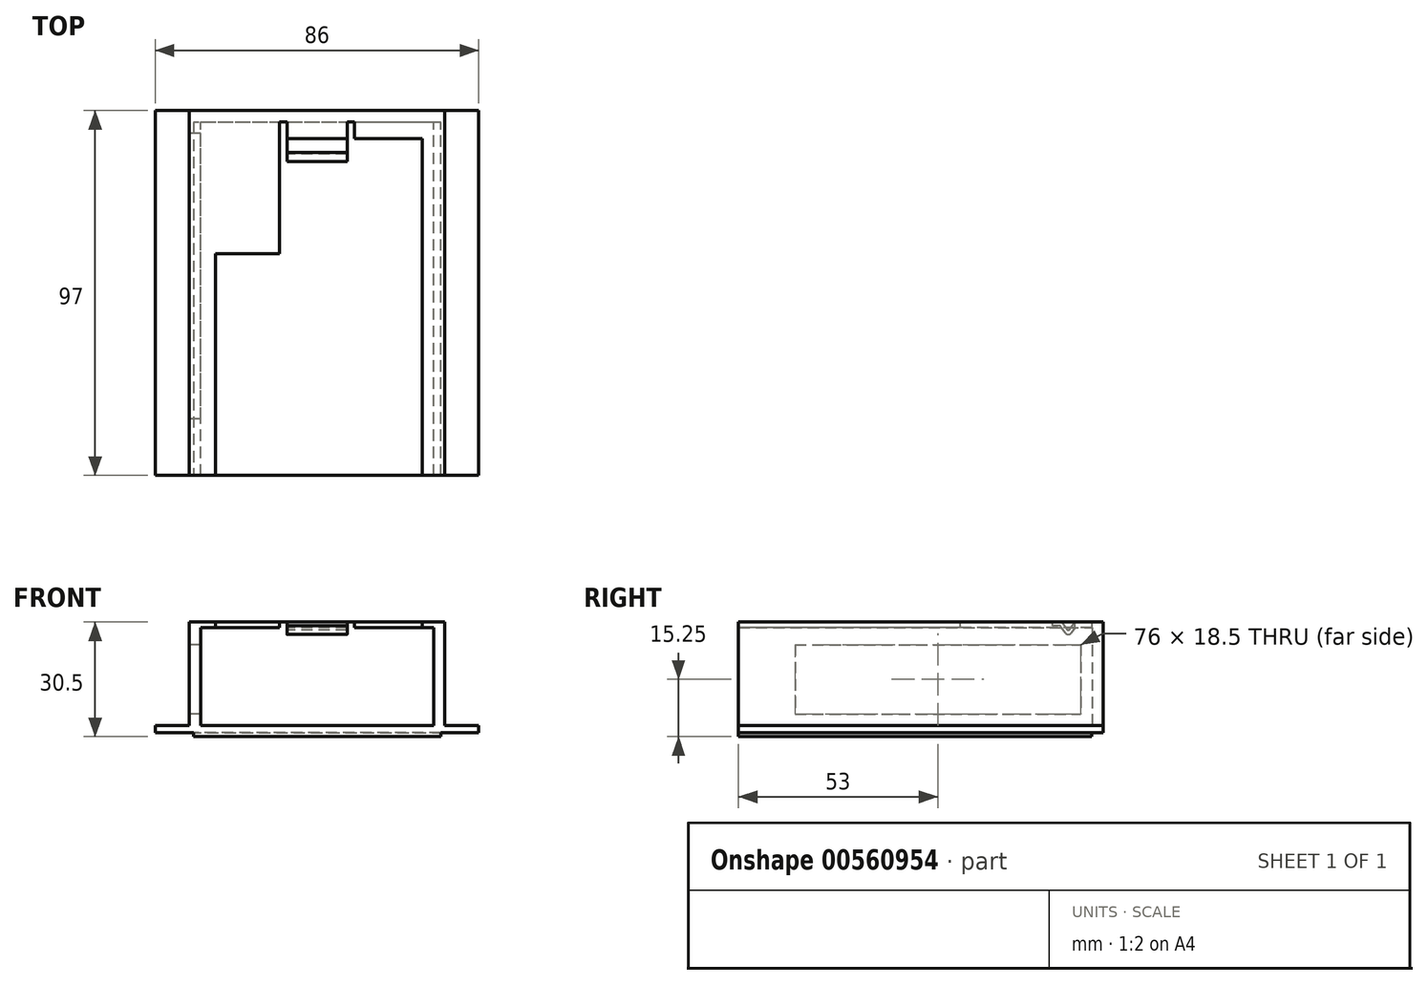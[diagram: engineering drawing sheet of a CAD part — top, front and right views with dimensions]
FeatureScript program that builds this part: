
annotation { "Feature Type Name" : "Feature", "Feature Type Description" : "" }
export const myFeature = defineFeature(function(context is Context, id is Id, definition is map)
    precondition{}
    {
        {
            var Q0;
            Q0=qCreatedBy(makeId("Top.planeOp"),FACE);
            var sketch = newSketch(context, id + "F0", { "sketchPlane" : qUnion([Q0])});
            skLineSegment(sketch, "E0.top", {"start": v(0, 97) * mm, "end": v(86, 97) * mm});
            skLineSegment(sketch, "E0.left", {"start": v(0, 0) * mm, "end": v(0, 97) * mm});
            skLineSegment(sketch, "E0.right", {"start": v(86, 0) * mm, "end": v(86, 97) * mm});
            skLineSegment(sketch, "E1", {"start": v(0, 0) * mm, "end": v(86, 0) * mm});
            skSolve(sketch);
        }
        {
            var Q0;
            Q0=makeQuery(id+"F0.imprint","IMPRINT",FACE,{"disambiguationData":[TD([[makeQuery(id+"F0.imprint","IMPRINT",EDGE,{"derivedFrom":sQuery(id+"F0.wireOp",EDGE,"E0.top")}),-1.0]])]});
            extrude(context, id + "F1", {"entities" : qUnion([Q0]), "depth" : 3 * mm, "offsetDistance" : 25 * mm});
        }
        {
            var Q0;
            Q0=makeQuery(id+"F1.opExtrude","CAP_FACE",FACE,{"disambiguationData":[OSD([sQuery(id+"F0.wireOp",EDGE,"E0.top"),sQuery(id+"F0.wireOp",EDGE,"E0.left"),sQuery(id+"F0.wireOp",EDGE,"E0.right"),sQuery(id+"F0.wireOp",EDGE,"E1")])],"isStart":false});
            var sketch = newSketch(context, id + "F2", { "sketchPlane" : qUnion([Q0])});
            skLineSegment(sketch, "E2.bottom", {"start": v(9, 0) * mm, "end": v(77, 0) * mm});
            skLineSegment(sketch, "E2.top", {"start": v(9, 97) * mm, "end": v(77, 97) * mm});
            skLineSegment(sketch, "E2.left", {"start": v(9, 0) * mm, "end": v(9, 97) * mm});
            skLineSegment(sketch, "E2.right", {"start": v(77, 0) * mm, "end": v(77, 97) * mm});
            skLineSegment(sketch, "E3", {"start": v(77, 97) * mm, "end": v(86, 97) * mm, "construction": true});
            skLineSegment(sketch, "E4", {"start": v(9, 97) * mm, "end": v(0, 97) * mm, "construction": true});
            skSolve(sketch);
        }
        {
            var Q0;
            Q0=makeQuery(id+"F2.imprint","IMPRINT",FACE,{"disambiguationData":[TD([[makeQuery(id+"F2.imprint","IMPRINT",EDGE,{"derivedFrom":sQuery(id+"F2.wireOp",EDGE,"E2.bottom")}),1.0]])]});
            extrude(context, id + "F3", {"entities" : qUnion([Q0]), "operationType" : NewBodyOperationType.ADD, "depth" : 27.5 * mm, "offsetDistance" : 25 * mm});
        }
        {
            var Q0;
            Q0=makeQuery(id+"F3.opExtrude","CAP_FACE",FACE,{"disambiguationData":[OSD([sQuery(id+"F2.wireOp",EDGE,"E2.bottom"),sQuery(id+"F2.wireOp",EDGE,"E2.top"),sQuery(id+"F2.wireOp",EDGE,"E2.left"),sQuery(id+"F2.wireOp",EDGE,"E2.right")])],"isStart":false});
            var Q1;
            Q1=makeQuery(id+"F3.boolean.opBoolean","MERGE",FACE,{"derivedFrom":[makeQuery(id+"F1.opExtrude","SWEPT_FACE",FACE,{"disambiguationData":[OSD([sQuery(id+"F0.wireOp",EDGE,"E1")])]}),makeQuery(id+"F3.opExtrude","SWEPT_FACE",FACE,{"disambiguationData":[OSD([sQuery(id+"F2.wireOp",EDGE,"E2.bottom")])]})]});
            shell(context, id + "F4", {"entities" : qUnion([Q0, Q1]), "thickness" : 3 * mm});
        }
        {
            var Q0;
            Q0=makeQuery(id+"F4.opShell","OFFSET_FACE",FACE,{"disambiguationData":[OSD([sQuery(id+"F2.wireOp",EDGE,"E2.left")])]});
            var Q1;
            Q1=makeQuery(id+"F4.opShell","OFFSET_FACE",FACE,{"disambiguationData":[OSD([sQuery(id+"F2.wireOp",EDGE,"E2.right")])]});
            cPlane(context, id + "F5", {"entities" : qUnion([Q0, Q1]), "cplaneType" : CPlaneType.MID_PLANE, "offset" : 25 * mm, "width" : 150 * mm, "height" : 150 * mm});
        }
        {
            var Q0;
            Q0=qCreatedBy(id+"F5.planeOp",FACE);
            var sketch = newSketch(context, id + "F6", { "sketchPlane" : qUnion([Q0])});
            skLineSegment(sketch, "E5.bottom", {"start": v(94, 30.5) * mm, "end": v(89.5, 30.5) * mm});
            skLineSegment(sketch, "E5.top", {"start": v(94, 29) * mm, "end": v(89.5, 29) * mm});
            skLineSegment(sketch, "E5.left", {"start": v(94, 30.5) * mm, "end": v(94, 29) * mm});
            skLineSegment(sketch, "E6.0", {"start": v(94, 30.5) * mm, "end": v(94, 3) * mm, "construction": true});
            skLineSegment(sketch, "E7", {"start": v(89.5, 29) * mm, "end": v(88.5, 27.61) * mm});
            skLineSegment(sketch, "E8", {"start": v(86.87, 27.61) * mm, "end": v(85.5, 29.5) * mm});
            skLineSegment(sketch, "E9", {"start": v(85.5, 29.5) * mm, "end": v(83.5, 29.5) * mm});
            skLineSegment(sketch, "E10", {"start": v(83.5, 29.5) * mm, "end": v(83.5, 30.5) * mm});
            skLineSegment(sketch, "E11", {"start": v(83.5, 30.5) * mm, "end": v(85.86, 30.5) * mm});
            skLineSegment(sketch, "E12", {"start": v(85.86, 30.5) * mm, "end": v(87.28, 28.56) * mm});
            skLineSegment(sketch, "E13", {"start": v(88.09, 28.56) * mm, "end": v(89.5, 30.5) * mm});
            skLineSegment(sketch, "E14", {"start": v(87.68, 28) * mm, "end": v(87.68, 30.5) * mm, "construction": true});
            skLineSegment(sketch, "E15", {"start": v(87.68, 30.5) * mm, "end": v(85.86, 30.5) * mm, "construction": true});
            skLineSegment(sketch, "E16", {"start": v(89.5, 30.5) * mm, "end": v(87.68, 30.5) * mm, "construction": true});
            skPoint(sketch, "E17.visualSharp", {"position": v(87.68, 26.5) * mm});
            skArc(sketch, "E17.filletArc", {"start": v(86.87, 27.61) * mm, "mid": v(87.68, 27.2) * mm, "end": v(88.5, 27.61) * mm});
            skPoint(sketch, "E18.visualSharp", {"position": v(87.68, 28) * mm});
            skArc(sketch, "E18.filletArc", {"start": v(87.28, 28.56) * mm, "mid": v(87.68, 28.35) * mm, "end": v(88.09, 28.56) * mm});
            skSolve(sketch);
        }
        {
            var Q0;
            Q0=makeQuery(id+"F6.imprint","IMPRINT",FACE,{"disambiguationData":[TD([[makeQuery(id+"F6.imprint","IMPRINT",EDGE,{"derivedFrom":sQuery(id+"F6.wireOp",EDGE,"E5.bottom")}),1.0]])]});
            extrude(context, id + "F7", {"entities" : qUnion([Q0]), "operationType" : NewBodyOperationType.ADD, "endBound" : BoundingType.SYMMETRIC, "depth" : 16 * mm, "offsetDistance" : 25 * mm});
        }
        {
            var Q0;
            Q0=makeQuery(id+"F7.boolean.opBoolean","MERGE",FACE,{"derivedFrom":[makeQuery(id+"F3.opExtrude","CAP_FACE",FACE,{"disambiguationData":[OSD([sQuery(id+"FaPYS6YZykbCoQc_1.wireOp",EDGE,"4SR8hnLx-uEol-jzUZ-u4qq-Ke9y254ZlhNw.bottom"),sQuery(id+"FaPYS6YZykbCoQc_1.wireOp",EDGE,"4SR8hnLx-uEol-jzUZ-u4qq-Ke9y254ZlhNw.top"),sQuery(id+"FaPYS6YZykbCoQc_1.wireOp",EDGE,"4SR8hnLx-uEol-jzUZ-u4qq-Ke9y254ZlhNw.left"),sQuery(id+"FaPYS6YZykbCoQc_1.wireOp",EDGE,"4SR8hnLx-uEol-jzUZ-u4qq-Ke9y254ZlhNw.right")])],"isStart":false}),makeQuery(id+"F7.opExtrude","SWEPT_FACE",FACE,{"disambiguationData":[OSD([sQuery(id+"F6.wireOp",EDGE,"E5.bottom")])]})]});
            var sketch = newSketch(context, id + "F8", { "sketchPlane" : qUnion([Q0])});
            skLineSegment(sketch, "E19.bottom", {"start": v(53, 94) * mm, "end": v(59, 94) * mm});
            skLineSegment(sketch, "E20.bottom", {"start": v(12, 94) * mm, "end": v(33, 94) * mm});
            skLineSegment(sketch, "E20.top", {"start": v(16, 59) * mm, "end": v(33, 59) * mm});
            skLineSegment(sketch, "E20.left", {"start": v(12, 94) * mm, "end": v(12, 59) * mm});
            skLineSegment(sketch, "E20.right", {"start": v(33, 94) * mm, "end": v(33, 59) * mm});
            skLineSegment(sketch, "E21.top", {"start": v(12, 0) * mm, "end": v(16, 0) * mm});
            skLineSegment(sketch, "E21.left", {"start": v(12, 59) * mm, "end": v(12, 0) * mm});
            skLineSegment(sketch, "E21.right", {"start": v(16, 59) * mm, "end": v(16, 0) * mm});
            skLineSegment(sketch, "E22.bottom", {"start": v(53, 94) * mm, "end": v(74, 94) * mm});
            skLineSegment(sketch, "E22.top", {"start": v(53, 89.5) * mm, "end": v(71, 89.5) * mm});
            skLineSegment(sketch, "E22.left", {"start": v(53, 94) * mm, "end": v(53, 89.5) * mm});
            skLineSegment(sketch, "E22.right", {"start": v(74, 94) * mm, "end": v(74, 89.5) * mm});
            skLineSegment(sketch, "E23.bottom", {"start": v(74, 94) * mm, "end": v(71, 94) * mm});
            skLineSegment(sketch, "E23.top", {"start": v(74, 0) * mm, "end": v(71, 0) * mm});
            skLineSegment(sketch, "E23.left", {"start": v(74, 94) * mm, "end": v(74, 0) * mm});
            skLineSegment(sketch, "E23.right", {"start": v(71, 89.5) * mm, "end": v(71, 0) * mm});
            skSolve(sketch);
        }
        {
            var Q0;
            Q0=makeQuery(id+"F8.imprint","IMPRINT",FACE,{"disambiguationData":[TD([[makeQuery(id+"F8.imprint","IMPRINT",EDGE,{"derivedFrom":sQuery(id+"F8.wireOp",EDGE,"E20.bottom")}),-1.0]])]});
            var Q1;
            Q1=makeQuery(id+"F8.imprint","IMPRINT",FACE,{"disambiguationData":[TD([[makeQuery(id+"F8.imprint","IMPRINT",EDGE,{"derivedFrom":sQuery(id+"F8.wireOp",EDGE,"E22.top")}),1.0]])]});
            extrude(context, id + "F9", {"entities" : qUnion([Q0, Q1]), "operationType" : NewBodyOperationType.ADD, "oppositeDirection" : true, "depth" : 1.5 * mm, "offsetDistance" : 25 * mm});
        }
        {
            var Q0;
            Q0=makeQuery(id+"F3.opExtrude","SWEPT_FACE",FACE,{"disambiguationData":[OSD([sQuery(id+"F2.wireOp",EDGE,"E2.left")])]});
            var sketch = newSketch(context, id + "F10", { "sketchPlane" : qUnion([Q0])});
            skLineSegment(sketch, "E24.bottom", {"start": v(-91, 6) * mm, "end": v(-15, 6) * mm});
            skLineSegment(sketch, "E24.top", {"start": v(-91, 24.5) * mm, "end": v(-15, 24.5) * mm});
            skLineSegment(sketch, "E24.left", {"start": v(-91, 6) * mm, "end": v(-91, 24.5) * mm});
            skLineSegment(sketch, "E24.right", {"start": v(-15, 6) * mm, "end": v(-15, 24.5) * mm});
            skSolve(sketch);
        }
        {
            var Q0;
            Q0=makeQuery(id+"F10.imprint","IMPRINT",FACE,{"disambiguationData":[TD([[makeQuery(id+"F10.imprint","IMPRINT",EDGE,{"derivedFrom":sQuery(id+"F10.wireOp",EDGE,"E24.bottom")}),1.0]])]});
            extrude(context, id + "F11", {"entities" : qUnion([Q0]), "operationType" : NewBodyOperationType.REMOVE, "endBound" : BoundingType.UP_TO_NEXT, "oppositeDirection" : true, "depth" : 25 * mm, "offsetDistance" : 25 * mm});
        }
        {
            var Q0;
            Q0=makeQuery(id+"F1.opExtrude","CAP_FACE",FACE,{"disambiguationData":[OSD([sQuery(id+"F0.wireOp",EDGE,"E0.top"),sQuery(id+"F0.wireOp",EDGE,"E0.left"),sQuery(id+"F0.wireOp",EDGE,"E0.right"),sQuery(id+"F0.wireOp",EDGE,"E1")])],"isStart":true});
            var sketch = newSketch(context, id + "F12", { "sketchPlane" : qUnion([Q0])});
            skLineSegment(sketch, "E25.bottom", {"start": v(0, -97) * mm, "end": v(10.1, -97) * mm});
            skLineSegment(sketch, "E25.top", {"start": v(0, 0) * mm, "end": v(10.1, 0) * mm});
            skLineSegment(sketch, "E25.left", {"start": v(0, -97) * mm, "end": v(0, 0) * mm});
            skLineSegment(sketch, "E25.right", {"start": v(10.1, -93.9) * mm, "end": v(10.1, 0) * mm});
            skLineSegment(sketch, "E26.bottom", {"start": v(86, 0) * mm, "end": v(75.9, 0) * mm});
            skLineSegment(sketch, "E26.top", {"start": v(86, -97) * mm, "end": v(75.9, -97) * mm});
            skLineSegment(sketch, "E26.left", {"start": v(86, 0) * mm, "end": v(86, -97) * mm});
            skLineSegment(sketch, "E26.right", {"start": v(75.9, 0) * mm, "end": v(75.9, -93.9) * mm});
            skLineSegment(sketch, "E27.bottom", {"start": v(75.9, -97) * mm, "end": v(10.1, -97) * mm});
            skLineSegment(sketch, "E27.top", {"start": v(75.9, -93.9) * mm, "end": v(10.1, -93.9) * mm});
            skSolve(sketch);
        }
        {
            var Q0;
            Q0 = qSketchRegion(id + "F12", true);
            extrude(context, id + "F13", {"entities" : qUnion([Q0]), "operationType" : NewBodyOperationType.REMOVE, "oppositeDirection" : true, "depth" : 1.1 * mm, "offsetDistance" : 25 * mm});
        }
    });
